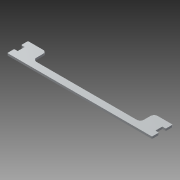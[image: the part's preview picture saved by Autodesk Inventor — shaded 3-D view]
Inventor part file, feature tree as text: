
AUTODESK INVENTOR PART (.ipt)
format: ipt  version: 2015 (Build 190159000, 159)  size: 131,072 bytes
history: native  units: mm
features: extrude x1, sketch x1
ambient origin geometry x8: Origin, YZ Plane, XZ Plane, XY Plane, X Axis, Y Axis, Z Axis, Center Point
bodies: Solid1 (feature_tree)
feature tree (2):
  extrude  "Extrusion1"  Depth=1.0mm
  sketch  "Sketch1"  dims[d0=10.0mm d2=1.0mm d3=3.0mm d4=0.0mm d8=27.0mm d9=10.0mm d10=5.0mm d11=5.0mm d12=1.0mm d13=27.0mm d14=5.0mm d15=10.0mm d16=10.0mm d17=30.0mm d18=1.0mm d19=30.0mm d20=210.0mm d21=5.0mm]
